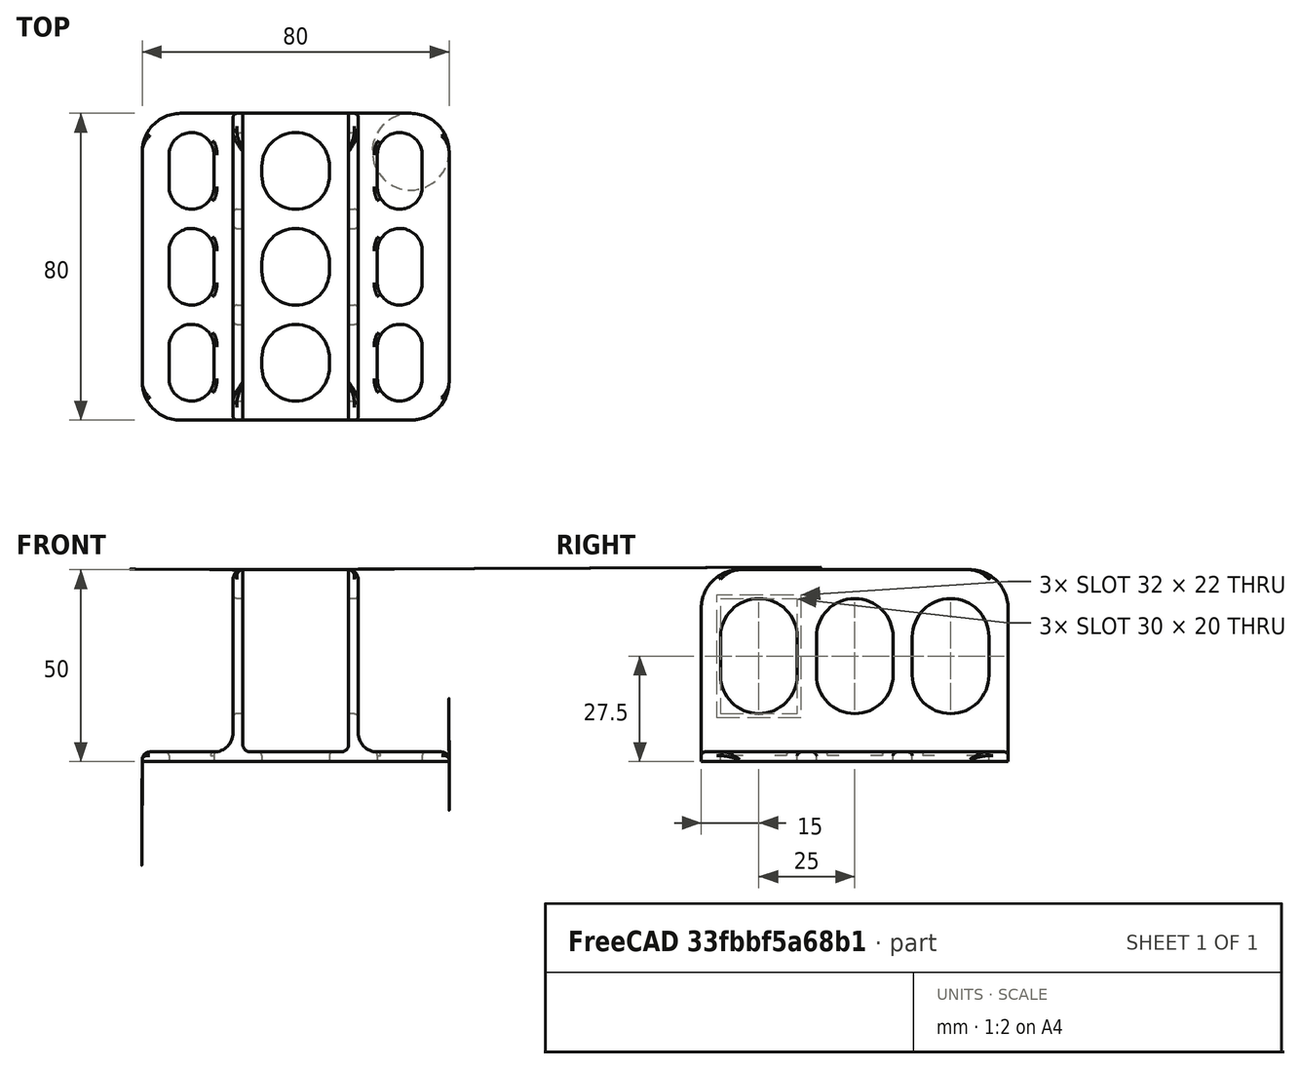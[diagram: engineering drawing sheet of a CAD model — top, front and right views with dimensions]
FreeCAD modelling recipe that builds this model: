
FCSTD DOCUMENT  (FreeCAD 1.0R39319 (Git))
Label: Charger Stand-2.2
License: Creative Commons Attribution 4.0
LicenseURL: https://creativecommons.org/licenses/by/4.0/
objects: Sketcher::SketchObject×5, PartDesign::Pocket×4, PartDesign::Pad×1, PartDesign::Fillet×1, PartDesign::Body×1
note: 29 computed .brp shape members not serialized (recipe doc carries the construction recipe); baked Part::Feature solids carry a one-line shape summary decoded from their .brp

FEATURE [Sketcher::SketchObject] Sketch
  ArcFitTolerance = 1e-06
  AttachmentSupport = -> [XZ_Plane]
  FullyConstrained = true
  MakeInternals = false
  MapMode = 5
  Placement = pos=(0,0,0) rot=(1,0,0;1.5708rad)
  sketch-geometry (18):
    g0: LineSegment StartX=-40 StartY=0 StartZ=0 EndX=40 EndY=0 EndZ=0
    g1: LineSegment StartX=38 StartY=2.5 StartZ=0 EndX=21.3 EndY=2.5 EndZ=0
    g2: LineSegment StartX=-38 StartY=2.5 StartZ=0 EndX=-21.3 EndY=2.5 EndZ=0
    g3: LineSegment StartX=-16.3 StartY=7.5 StartZ=0 EndX=-16.3 EndY=47.5 EndZ=0
    g4: LineSegment StartX=-13.8 StartY=50 StartZ=0 EndX=-13.8 EndY=4.5 EndZ=0
    g5: LineSegment StartX=-11.8 StartY=2.5 StartZ=0 EndX=11.8 EndY=2.5 EndZ=0
    g6: LineSegment StartX=13.8 StartY=4.5 StartZ=0 EndX=13.8 EndY=50 EndZ=0
    g7: LineSegment StartX=16.3 StartY=47.5 StartZ=0 EndX=16.3 EndY=7.5 EndZ=0
    g8: ArcOfCircle CenterX=-13.8 CenterY=47.5 CenterZ=0 NormalX=0 NormalY=0 NormalZ=1 AngleXU=0 Radius=2.5 StartAngle=1.5708 EndAngle=3.14159
    g9: ArcOfCircle CenterX=13.8 CenterY=47.5 CenterZ=0 NormalX=0 NormalY=0 NormalZ=1 AngleXU=0 Radius=2.5 StartAngle=-9e-16 EndAngle=1.5708
    g10: ArcOfCircle CenterX=21.3 CenterY=7.5 CenterZ=0 NormalX=0 NormalY=0 NormalZ=1 AngleXU=0 Radius=5 StartAngle=3.14159 EndAngle=4.71239
    g11: ArcOfCircle CenterX=11.8 CenterY=4.5 CenterZ=0 NormalX=0 NormalY=0 NormalZ=1 AngleXU=0 Radius=2 StartAngle=4.71239 EndAngle=6.28319
    g12: ArcOfCircle CenterX=-11.8 CenterY=4.5 CenterZ=0 NormalX=0 NormalY=0 NormalZ=1 AngleXU=0 Radius=2 StartAngle=3.14159 EndAngle=4.71239
    g13: ArcOfCircle CenterX=-21.3 CenterY=7.5 CenterZ=0 NormalX=0 NormalY=0 NormalZ=1 AngleXU=0 Radius=5 StartAngle=4.71239 EndAngle=6.28319
    g14: LineSegment StartX=40 StartY=0 StartZ=0 EndX=40 EndY=0.5 EndZ=0
    g15: LineSegment StartX=-40 StartY=0 StartZ=0 EndX=-40 EndY=0.5 EndZ=0
    g16: ArcOfCircle CenterX=38 CenterY=0.5 CenterZ=0 NormalX=0 NormalY=0 NormalZ=1 AngleXU=0 Radius=2 StartAngle=0 EndAngle=1.5708
    g17: ArcOfCircle CenterX=-38 CenterY=0.5 CenterZ=0 NormalX=0 NormalY=0 NormalZ=1 AngleXU=0 Radius=2 StartAngle=1.5708 EndAngle=3.14159
  constraints (47):
    c: PointOnObject(g0,g-1)
    c: Horizontal(g1)
    c: Horizontal(g2)
    c: Vertical(g3)
    c: Vertical(g4)
    c: Horizontal(g5)
    c: Vertical(g6)
    c: Vertical(g7)
    c: Coincident(g8,g4)
    c: Coincident(g9,g6)
    c: Symmetric(g0,g0,g-2)
    c: Tangent(g10,g1) = 1.5708
    c: Tangent(g10,g7) = -1.5708
    c: Tangent(g11,g6) = -1.5708
    c: Tangent(g11,g5) = -1.5708
    c: Tangent(g12,g5) = -1.5708
    c: Tangent(g12,g4) = -1.5708
    c: Tangent(g13,g3) = -1.5708
    c: Tangent(g13,g2) = -1.5708
    c: Tangent(g8,g3) = 1.5708
    c: Perpendicular(g8,g4)
    c: Perpendicular(g9,g6)
    c: Tangent(g9,g7) = 1.5708
    c: Coincident(g14,g0)
    c: Coincident(g15,g0)
    c: Vertical(g15)
    c: Tangent(g17,g15) = 1.5708
    c: Tangent(g17,g2) = 1.5708
    c: Tangent(g16,g14) = -1.5708
    c: Tangent(g16,g1) = -1.5708
    c: Vertical(g14)
    c: Equal(g14,g15)
    c: Equal(g17,g12)
    c: Equal(g12,g11)
    c: Equal(g11,g16)
    c: Equal(g8,g9)
    c: Equal(g2,g1)
    c: Equal(g7,g3)
    c: Equal(g4,g6)
    c: Radius(g16) = 2
    c: DistanceY(g1) = 2.5
    c: DistanceX(g4,g6) = 27.6
    c: Radius(g9) = 2.5
    c: Radius(g10) = 5
    c: Horizontal(g5,g1)
    c: DistanceY(g6) = 50
    c: DistanceX(g0,g0) = 80
FEATURE [PartDesign::Pad] Pad
  Direction = (0,-1,2e-16)
  Length = 80
  Length2 = 10
  Midplane = true
  Placement = pos=(0,0,0) rot=(1,0,0;1.5708rad)
  Profile = -> Sketch
  ReferenceAxis = -> Sketch [N_Axis]
  Refine = true
  Suppressed = false
  Type = 0
FEATURE [Sketcher::SketchObject] Sketch001
  ArcFitTolerance = 1e-06
  AttachmentSupport = -> [Pad]
  ExternalGeometry = -> [Pad]
  FullyConstrained = true
  MakeInternals = false
  MapMode = 5
  Placement = pos=(16.3,0,0) rot=(0.707107,0,0.707107;3.14159rad)
  sketch-geometry (6):
    g0: LineSegment StartX=50 StartY=40 StartZ=0 EndX=40 EndY=40 EndZ=0
    g1: LineSegment StartX=50 StartY=40 StartZ=0 EndX=50 EndY=30 EndZ=0
    g2: LineSegment StartX=50 StartY=-40 StartZ=0 EndX=50 EndY=-30 EndZ=0
    g3: LineSegment StartX=50 StartY=-40 StartZ=0 EndX=40 EndY=-40 EndZ=0
    g4: ArcOfCircle CenterX=40 CenterY=30 CenterZ=0 NormalX=0 NormalY=0 NormalZ=1 AngleXU=0 Radius=10 StartAngle=0 EndAngle=1.5708
    g5: ArcOfCircle CenterX=40 CenterY=-30 CenterZ=0 NormalX=0 NormalY=0 NormalZ=1 AngleXU=0 Radius=10 StartAngle=4.71239 EndAngle=6.28319
  constraints (17):
    c: Coincident(g0,g-3)
    c: Horizontal(g0)
    c: Coincident(g1,g0)
    c: PointOnObject(g1,g-3)
    c: Coincident(g2,g-3)
    c: PointOnObject(g2,g-3)
    c: Coincident(g3,g2)
    c: Horizontal(g3)
    c: Equal(g2,g3)
    c: Equal(g3,g1)
    c: Equal(g1,g0)
    c: Coincident(g4,g0)
    c: Coincident(g5,g2)
    c: Coincident(g5,g3)
    c: Tangent(g4,g1) = 1.5708
    c: Radius(g4) = 10
    c: Equal(g5,g4)
FEATURE [PartDesign::Pocket] Pocket
  BaseFeature = -> Pad
  Direction = (-1,0,2e-16)
  Length = 5
  Length2 = 5
  Placement = pos=(0,0,0) rot=(1,0,0;1.5708rad)
  Profile = -> Sketch001
  ReferenceAxis = -> Sketch001 [N_Axis]
  Refine = true
  Suppressed = false
  Type = 1
FEATURE [Sketcher::SketchObject] Sketch002
  ArcFitTolerance = 1e-06
  AttachmentSupport = -> [Pocket]
  ExternalGeometry = -> [Pocket]
  FullyConstrained = true
  MakeInternals = false
  MapMode = 5
  Placement = pos=(0,1.1e-15,2.5) rot=(0,0,1;3.14159rad)
  sketch-geometry (12):
    g0: LineSegment StartX=-40 StartY=30 StartZ=0 EndX=-40 EndY=40 EndZ=0
    g1: LineSegment StartX=-40 StartY=40 StartZ=0 EndX=-30 EndY=40 EndZ=0
    g2: LineSegment StartX=30 StartY=40 StartZ=0 EndX=40 EndY=40 EndZ=0
    g3: LineSegment StartX=40 StartY=40 StartZ=0 EndX=40 EndY=30 EndZ=0
    g4: LineSegment StartX=40 StartY=-30 StartZ=0 EndX=40 EndY=-40 EndZ=0
    g5: LineSegment StartX=40 StartY=-40 StartZ=0 EndX=30 EndY=-40 EndZ=0
    g6: LineSegment StartX=-40 StartY=-40 StartZ=0 EndX=-40 EndY=-30 EndZ=0
    g7: LineSegment StartX=-40 StartY=-40 StartZ=0 EndX=-30 EndY=-40 EndZ=0
    g8: ArcOfCircle CenterX=-30 CenterY=30 CenterZ=0 NormalX=0 NormalY=0 NormalZ=1 AngleXU=0 Radius=10 StartAngle=1.5708 EndAngle=3.14159
    g9: ArcOfCircle CenterX=30 CenterY=30 CenterZ=0 NormalX=0 NormalY=0 NormalZ=1 AngleXU=0 Radius=10 StartAngle=3e-16 EndAngle=1.5708
    g10: ArcOfCircle CenterX=30 CenterY=-30 CenterZ=0 NormalX=0 NormalY=0 NormalZ=1 AngleXU=0 Radius=10 StartAngle=4.71239 EndAngle=6.28319
    g11: ArcOfCircle CenterX=-30 CenterY=-30 CenterZ=0 NormalX=0 NormalY=0 NormalZ=1 AngleXU=0 Radius=10 StartAngle=3.14159 EndAngle=4.71239
  constraints (35):
    c: PointOnObject(g0,g-4)
    c: Coincident(g0,g-4)
    c: Coincident(g1,g0)
    c: Horizontal(g1)
    c: Coincident(g2,g-3)
    c: Horizontal(g2)
    c: Coincident(g3,g2)
    c: PointOnObject(g3,g-3)
    c: PointOnObject(g4,g-3)
    c: Coincident(g4,g-3)
    c: Coincident(g5,g4)
    c: Horizontal(g5)
    c: Coincident(g6,g-4)
    c: PointOnObject(g6,g-4)
    c: Coincident(g7,g6)
    c: Horizontal(g7)
    c: Equal(g7,g6)
    c: Equal(g6,g0)
    c: Equal(g0,g1)
    c: Equal(g1,g2)
    c: Equal(g2,g3)
    c: Equal(g3,g4)
    c: Equal(g4,g5)
    c: Coincident(g8,g0)
    c: Coincident(g8,g1)
    c: Coincident(g9,g2)
    c: Coincident(g9,g3)
    c: Coincident(g10,g5)
    c: Coincident(g11,g6)
    c: Coincident(g11,g7)
    c: Equal(g11,g8)
    c: Equal(g8,g9)
    c: Equal(g9,g10)
    c: Tangent(g10,g4) = 1.5708
    c: Radius(g9) = 10
FEATURE [PartDesign::Pocket] Pocket001
  BaseFeature = -> Pocket
  Direction = (0,0,-1)
  Length = 5
  Length2 = 5
  Placement = pos=(0,0,0) rot=(1,0,0;1.5708rad)
  Profile = -> Sketch002
  ReferenceAxis = -> Sketch002 [N_Axis]
  Refine = true
  Suppressed = false
  Type = 1
FEATURE [Sketcher::SketchObject] Sketch003
  ArcFitTolerance = 1e-06
  AttachmentSupport = -> [Pocket001]
  ExternalGeometry = -> [Pocket001]
  FullyConstrained = true
  MakeInternals = false
  MapMode = 5
  Placement = pos=(-16.3,0,0) rot=(0.707107,0,-0.707107;3.14159rad)
  sketch-geometry (17):
    g0: ArcOfCircle CenterX=-32.5 CenterY=25 CenterZ=0 NormalX=0 NormalY=0 NormalZ=1 AngleXU=0 Radius=10 StartAngle=1.5708 EndAngle=4.71239
    g1: ArcOfCircle CenterX=-22.5 CenterY=25 CenterZ=0 NormalX=0 NormalY=0 NormalZ=1 AngleXU=0 Radius=10 StartAngle=4.71239 EndAngle=7.85398
    g2: LineSegment StartX=-32.5 StartY=35 StartZ=0 EndX=-22.5 EndY=35 EndZ=0
    g3: LineSegment StartX=-32.5 StartY=15 StartZ=0 EndX=-22.5 EndY=15 EndZ=0
    g4: ArcOfCircle CenterX=-32.5 CenterY=0 CenterZ=0 NormalX=0 NormalY=0 NormalZ=1 AngleXU=0 Radius=10 StartAngle=1.5708 EndAngle=4.71239
    g5: ArcOfCircle CenterX=-22.5 CenterY=-9e-16 CenterZ=0 NormalX=0 NormalY=0 NormalZ=1 AngleXU=0 Radius=10 StartAngle=4.71239 EndAngle=7.85398
    g6: LineSegment StartX=-32.5 StartY=10 StartZ=0 EndX=-22.5 EndY=10 EndZ=0
    g7: LineSegment StartX=-32.5 StartY=-10 StartZ=0 EndX=-22.5 EndY=-10 EndZ=0
    g8: ArcOfCircle CenterX=-32.5 CenterY=-25 CenterZ=0 NormalX=0 NormalY=0 NormalZ=1 AngleXU=0 Radius=10 StartAngle=1.5708 EndAngle=4.71239
    g9: ArcOfCircle CenterX=-22.5 CenterY=-25 CenterZ=0 NormalX=0 NormalY=0 NormalZ=1 AngleXU=0 Radius=10 StartAngle=4.71239 EndAngle=7.85398
    g10: LineSegment StartX=-32.5 StartY=-15 StartZ=0 EndX=-22.5 EndY=-15 EndZ=0
    g11: LineSegment StartX=-32.5 StartY=-35 StartZ=0 EndX=-22.5 EndY=-35 EndZ=0
    g12: LineSegment [constr] StartX=-22.5 StartY=-9e-16 StartZ=0 EndX=-7.5 EndY=-9e-16 EndZ=0
    g13: LineSegment [constr] StartX=-32.5 StartY=0 StartZ=0 EndX=-47.5 EndY=0 EndZ=0
    g14: LineSegment [constr] StartX=-32.5 StartY=10 StartZ=0 EndX=-32.5 EndY=15 EndZ=0
    g15: LineSegment [constr] StartX=-32.5 StartY=35 StartZ=0 EndX=-32.5 EndY=40 EndZ=0
    g16: LineSegment [constr] StartX=-12.5 StartY=25 StartZ=0 EndX=-7.5 EndY=25 EndZ=0
  constraints (44):
    c: Tangent(g0,g2) = 1.5708
    c: Tangent(g0,g3) = -1.5708
    c: Tangent(g1,g2) = 1.5708
    c: Tangent(g1,g3) = -1.5708
    c: Equal(g0,g1)
    c: Horizontal(g2)
    c: Tangent(g4,g6) = 1.5708
    c: Tangent(g4,g7) = -1.5708
    c: Tangent(g5,g6) = 1.5708
    c: Tangent(g5,g7) = -1.5708
    c: Equal(g4,g5)
    c: Horizontal(g7)
    c: PointOnObject(g4,g-1)
    c: Tangent(g8,g10) = 1.5708
    c: Tangent(g8,g11) = -1.5708
    c: Tangent(g9,g10) = 1.5708
    c: Tangent(g9,g11) = -1.5708
    c: Equal(g8,g9)
    c: Equal(g5,g1)
    c: Equal(g1,g9)
    c: Vertical(g9,g5)
    c: Vertical(g8,g4)
    c: Vertical(g4,g0)
    c: Horizontal(g11)
    c: Coincident(g12,g5)
    c: PointOnObject(g12,g-5)
    c: Coincident(g13,g4)
    c: PointOnObject(g13,g-4)
    c: Coincident(g14,g4)
    c: Coincident(g14,g0)
    c: Coincident(g15,g0)
    c: PointOnObject(g15,g-3)
    c: Vertical(g15)
    c: Equal(g14,g15)
    c: Horizontal(g12)
    c: Horizontal(g13)
    c: Equal(g13,g12)
    c: Symmetric(g1,g9,g-1)
    c: DistanceY(g15,g15) = 5
    c: PointOnObject(g16,g1)
    c: PointOnObject(g16,g-5)
    c: Horizontal(g16)
    c: Perpendicular(g1,g16)
    c: Equal(g16,g15)
FEATURE [PartDesign::Pocket] Pocket002
  BaseFeature = -> Pocket001
  Direction = (1,0,2e-16)
  Length = 5
  Length2 = 5
  Placement = pos=(0,0,0) rot=(1,0,0;1.5708rad)
  Profile = -> Sketch003
  ReferenceAxis = -> Sketch003 [N_Axis]
  Refine = true
  Suppressed = false
  Type = 1
FEATURE [Sketcher::SketchObject] Sketch004
  ArcFitTolerance = 1e-06
  AttachmentSupport = -> [Pocket002]
  ExternalGeometry = -> [Pocket002]
  FullyConstrained = true
  MakeInternals = false
  MapMode = 5
  Placement = pos=(0,1.1e-15,2.5) rot=(0,0,1;3.14159rad)
  sketch-geometry (44):
    g0: ArcOfCircle CenterX=-27.15 CenterY=29.15 CenterZ=0 NormalX=0 NormalY=0 NormalZ=1 AngleXU=0 Radius=5.85 StartAngle=0 EndAngle=3.14159
    g1: ArcOfCircle CenterX=-27.15 CenterY=20.85 CenterZ=0 NormalX=0 NormalY=0 NormalZ=1 AngleXU=0 Radius=5.85 StartAngle=3.14159 EndAngle=6.28319
    g2: LineSegment StartX=-21.3 StartY=29.15 StartZ=0 EndX=-21.3 EndY=20.85 EndZ=0
    g3: LineSegment StartX=-33 StartY=29.15 StartZ=0 EndX=-33 EndY=20.85 EndZ=0
    g4: ArcOfCircle CenterX=27.15 CenterY=29.15 CenterZ=0 NormalX=0 NormalY=0 NormalZ=1 AngleXU=0 Radius=5.85 StartAngle=0 EndAngle=3.14159
    g5: ArcOfCircle CenterX=27.15 CenterY=20.85 CenterZ=0 NormalX=0 NormalY=0 NormalZ=1 AngleXU=0 Radius=5.85 StartAngle=3.14159 EndAngle=6.28319
    g6: LineSegment StartX=33 StartY=29.15 StartZ=0 EndX=33 EndY=20.85 EndZ=0
    g7: LineSegment StartX=21.3 StartY=29.15 StartZ=0 EndX=21.3 EndY=20.85 EndZ=0
    g8: LineSegment [constr] StartX=33 StartY=29.15 StartZ=0 EndX=38 EndY=29.15 EndZ=0
    g9: LineSegment [constr] StartX=21.3 StartY=29.15 StartZ=0 EndX=16.3 EndY=29.15 EndZ=0
    g10: LineSegment [constr] StartX=27.15 StartY=35 StartZ=0 EndX=27.15 EndY=40 EndZ=0
    g11: ArcOfCircle CenterX=-27.15 CenterY=4.15 CenterZ=0 NormalX=0 NormalY=0 NormalZ=1 AngleXU=0 Radius=5.85 StartAngle=2e-16 EndAngle=3.14159
    g12: ArcOfCircle CenterX=-27.15 CenterY=-4.15 CenterZ=0 NormalX=0 NormalY=0 NormalZ=1 AngleXU=0 Radius=5.85 StartAngle=3.14159 EndAngle=6.28319
    g13: LineSegment StartX=-21.3 StartY=4.15 StartZ=0 EndX=-21.3 EndY=-4.15 EndZ=0
    g14: LineSegment StartX=-33 StartY=4.15 StartZ=0 EndX=-33 EndY=-4.15 EndZ=0
    g15: ArcOfCircle CenterX=-27.15 CenterY=-20.85 CenterZ=0 NormalX=0 NormalY=0 NormalZ=1 AngleXU=0 Radius=5.85 StartAngle=2e-16 EndAngle=3.14159
    g16: ArcOfCircle CenterX=-27.15 CenterY=-29.15 CenterZ=0 NormalX=0 NormalY=0 NormalZ=1 AngleXU=0 Radius=5.85 StartAngle=3.14159 EndAngle=6.28319
    g17: LineSegment StartX=-21.3 StartY=-20.85 StartZ=0 EndX=-21.3 EndY=-29.15 EndZ=0
    g18: LineSegment StartX=-33 StartY=-20.85 StartZ=0 EndX=-33 EndY=-29.15 EndZ=0
    g19: ArcOfCircle CenterX=27.15 CenterY=4.15 CenterZ=0 NormalX=0 NormalY=0 NormalZ=1 AngleXU=0 Radius=5.85 StartAngle=2e-16 EndAngle=3.14159
    g20: ArcOfCircle CenterX=27.15 CenterY=-4.15 CenterZ=0 NormalX=0 NormalY=0 NormalZ=1 AngleXU=0 Radius=5.85 StartAngle=3.14159 EndAngle=6.28319
    g21: LineSegment StartX=33 StartY=4.15 StartZ=0 EndX=33 EndY=-4.15 EndZ=0
    g22: LineSegment StartX=21.3 StartY=4.15 StartZ=0 EndX=21.3 EndY=-4.15 EndZ=0
    g23: ArcOfCircle CenterX=27.15 CenterY=-20.85 CenterZ=0 NormalX=0 NormalY=0 NormalZ=1 AngleXU=0 Radius=5.85 StartAngle=2e-16 EndAngle=3.14159
    g24: ArcOfCircle CenterX=27.15 CenterY=-29.15 CenterZ=0 NormalX=0 NormalY=0 NormalZ=1 AngleXU=0 Radius=5.85 StartAngle=3.14159 EndAngle=6.28319
    g25: LineSegment StartX=33 StartY=-20.85 StartZ=0 EndX=33 EndY=-29.15 EndZ=0
    g26: LineSegment StartX=21.3 StartY=-20.85 StartZ=0 EndX=21.3 EndY=-29.15 EndZ=0
    g27: LineSegment [constr] StartX=27.15 StartY=10 StartZ=0 EndX=27.15 EndY=15 EndZ=0
    g28: ArcOfCircle CenterX=0 CenterY=26.2 CenterZ=0 NormalX=0 NormalY=0 NormalZ=1 AngleXU=0 Radius=8.8 StartAngle=3.18e-14 EndAngle=3.14159
    g29: ArcOfCircle CenterX=-7e-16 CenterY=23.8 CenterZ=0 NormalX=0 NormalY=0 NormalZ=1 AngleXU=0 Radius=8.8 StartAngle=3.14159 EndAngle=6.28319
    g30: LineSegment StartX=8.8 StartY=26.2 StartZ=0 EndX=8.8 EndY=23.8 EndZ=0
    g31: LineSegment StartX=-8.8 StartY=26.2 StartZ=0 EndX=-8.8 EndY=23.8 EndZ=0
    g32: ArcOfCircle CenterX=0 CenterY=1.2 CenterZ=0 NormalX=0 NormalY=0 NormalZ=1 AngleXU=0 Radius=8.8 StartAngle=1e-16 EndAngle=3.14159
    g33: ArcOfCircle CenterX=0 CenterY=-1.2 CenterZ=0 NormalX=0 NormalY=0 NormalZ=1 AngleXU=0 Radius=8.8 StartAngle=3.14159 EndAngle=6.28319
    g34: LineSegment StartX=8.8 StartY=1.2 StartZ=0 EndX=8.8 EndY=-1.2 EndZ=0
    g35: LineSegment StartX=-8.8 StartY=1.2 StartZ=0 EndX=-8.8 EndY=-1.2 EndZ=0
    g36: ArcOfCircle CenterX=-2e-16 CenterY=-23.8 CenterZ=0 NormalX=0 NormalY=0 NormalZ=1 AngleXU=0 Radius=8.8 StartAngle=0 EndAngle=3.14159
    g37: ArcOfCircle CenterX=0 CenterY=-26.2 CenterZ=0 NormalX=0 NormalY=0 NormalZ=1 AngleXU=0 Radius=8.8 StartAngle=3.14159 EndAngle=6.28319
    g38: LineSegment StartX=8.8 StartY=-23.8 StartZ=0 EndX=8.8 EndY=-26.2 EndZ=0
    g39: LineSegment StartX=-8.8 StartY=-23.8 StartZ=0 EndX=-8.8 EndY=-26.2 EndZ=0
    g40: LineSegment [constr] StartX=0 StartY=10 StartZ=0 EndX=0 EndY=15 EndZ=0
    g41: LineSegment [constr] StartX=-2e-16 StartY=-15 StartZ=0 EndX=-2e-16 EndY=-10 EndZ=0
    g42: LineSegment [constr] StartX=0 StartY=35 StartZ=0 EndX=0 EndY=40 EndZ=0
    g43: LineSegment [constr] StartX=8.8 StartY=26.2 StartZ=0 EndX=13.8 EndY=26.2 EndZ=0
  constraints (110):
    c: Tangent(g0,g2) = 1.5708
    c: Tangent(g0,g3) = -1.5708
    c: Tangent(g1,g2) = 1.5708
    c: Tangent(g1,g3) = -1.5708
    c: Equal(g0,g1)
    c: Vertical(g3)
    c: Tangent(g4,g6) = 1.5708
    c: Tangent(g4,g7) = -1.5708
    c: Tangent(g5,g6) = 1.5708
    c: Tangent(g5,g7) = -1.5708
    c: Equal(g4,g5)
    c: Symmetric(g4,g0,g-2)
    c: Equal(g0,g4)
    c: Horizontal(g1,g5)
    c: Coincident(g8,g4)
    c: PointOnObject(g8,g-3)
    c: Coincident(g9,g4)
    c: PointOnObject(g9,g-4)
    c: Horizontal(g9)
    c: Horizontal(g8)
    c: PointOnObject(g10,g4)
    c: Vertical(g10)
    c: Perpendicular(g4,g10)
    c: Horizontal(g10,g-4)
    c: Equal(g9,g8)
    c: Equal(g8,g10)
    c: DistanceX(g8,g8) = 5
    c: Vertical(g7)
    c: Tangent(g11,g13) = 1.5708
    c: Tangent(g11,g14) = -1.5708
    c: Tangent(g12,g13) = 1.5708
    c: Tangent(g12,g14) = -1.5708
    c: Equal(g11,g12)
    c: Tangent(g15,g17) = 1.5708
    c: Tangent(g15,g18) = -1.5708
    c: Tangent(g16,g17) = 1.5708
    c: Tangent(g16,g18) = -1.5708
    c: Equal(g15,g16)
    c: Tangent(g19,g21) = 1.5708
    c: Tangent(g19,g22) = -1.5708
    c: Tangent(g20,g21) = 1.5708
    c: Tangent(g20,g22) = -1.5708
    c: Equal(g19,g20)
    c: Tangent(g23,g25) = 1.5708
    c: Tangent(g23,g26) = -1.5708
    c: Tangent(g24,g25) = 1.5708
    c: Tangent(g24,g26) = -1.5708
    c: Equal(g23,g24)
    c: Equal(g5,g19)
    c: Equal(g19,g11)
    c: Equal(g11,g15)
    c: Equal(g15,g23)
    c: Vertical(g25)
    c: Vertical(g15,g12)
    c: Symmetric(g19,g11,g-2)
    c: Symmetric(g20,g12,g-2)
    c: Symmetric(g15,g23,g-2)
    c: Symmetric(g16,g24,g-2)
    c: Symmetric(g20,g19,g-1)
    c: PointOnObject(g27,g19)
    c: PointOnObject(g27,g5)
    c: Vertical(g27)
    c: Perpendicular(g19,g27)
    c: Equal(g27,g8)
    c: Equal(g25,g21)
    c: Equal(g21,g6)
    c: Symmetric(g23,g5,g-1)
    c: Tangent(g28,g30) = 1.5708
    c: Tangent(g28,g31) = -1.5708
    c: Tangent(g29,g30) = 1.5708
    c: Tangent(g29,g31) = -1.5708
    c: Equal(g28,g29)
    c: Vertical(g31)
    c: PointOnObject(g28,g-2)
    c: Tangent(g32,g34) = 1.5708
    c: Tangent(g32,g35) = -1.5708
    c: Tangent(g33,g34) = 1.5708
    c: Tangent(g33,g35) = -1.5708
    c: Equal(g32,g33)
    c: PointOnObject(g32,g-2)
    c: Tangent(g36,g38) = 1.5708
    c: Tangent(g36,g39) = -1.5708
    c: Tangent(g37,g38) = 1.5708
    c: Tangent(g37,g39) = -1.5708
    c: Equal(g36,g37)
    c: Vertical(g39)
    c: Equal(g36,g33)
    c: Equal(g33,g29)
    c: PointOnObject(g40,g32)
    c: PointOnObject(g40,g29)
    c: PointOnObject(g41,g36)
    c: PointOnObject(g41,g33)
    c: Vertical(g41)
    c: PointOnObject(g42,g28)
    c: Perpendicular(g28,g42)
    c: Vertical(g42)
    c: Perpendicular(g32,g40)
    c: Vertical(g40)
    c: Perpendicular(g36,g41)
    c: Equal(g40,g41)
    c: Equal(g41,g42)
    c: Equal(g42,g10)
    c: Horizontal(g-4,g42)
    c: Coincident(g43,g28)
    c: Horizontal(g43)
    c: Equal(g40,g43)
    c: Symmetric(g32,g33,g-1)
    c: Symmetric(g37,g28,g-1)
    c: Equal(g39,g35)
    c: PointOnObject(g43,g-5)
FEATURE [PartDesign::Pocket] Pocket003
  BaseFeature = -> Pocket002
  Direction = (0,0,-1)
  Length = 5
  Length2 = 5
  Placement = pos=(0,0,0) rot=(1,0,0;1.5708rad)
  Profile = -> Sketch004
  ReferenceAxis = -> Sketch004 [N_Axis]
  Refine = true
  Suppressed = false
  Type = 1
FEATURE [PartDesign::Fillet] Fillet
  Base = -> Pocket003 [Edge98,Edge97,Edge96,Edge81,Edge236,Edge232,Edge228,Edge94,Edge86,Edge176,Edge186,Edge182,Edge73,Edge166,Edge150,Edge134,Edge126,Edge142,Edge158]
  BaseFeature = -> Pocket003
  Placement = pos=(0,0,0) rot=(1,0,0;1.5708rad)
  Radius = 1
  Refine = true
  SupportTransform = false
  Suppressed = false
  UseAllEdges = false
FEATURE [PartDesign::Body] Body  label="Charger Stand"
  AllowCompound = false
  Group = -> [Sketch,Pad,Sketch001,Pocket,Sketch002,Pocket001,Sketch003,Pocket002,Sketch004,Pocket003,Fillet]
  Origin = -> Origin
  Tip = -> Fillet
